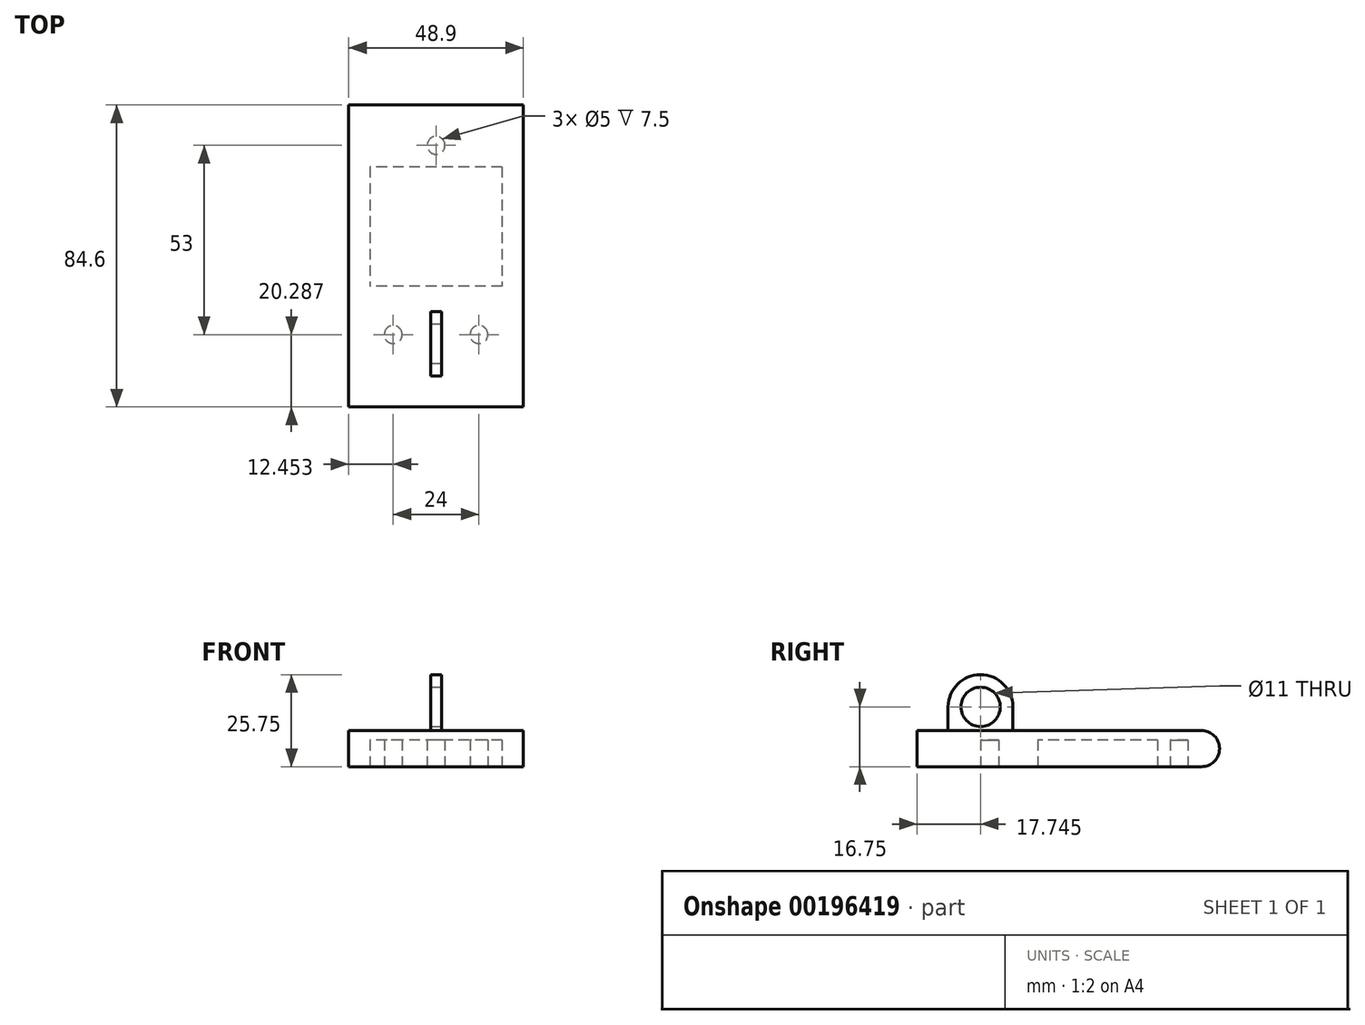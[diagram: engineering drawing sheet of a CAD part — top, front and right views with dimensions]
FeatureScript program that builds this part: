
annotation { "Feature Type Name" : "Feature", "Feature Type Description" : "" }
export const myFeature = defineFeature(function(context is Context, id is Id, definition is map)
    precondition{}
    {
        {
            var Q0;
            Q0=qCreatedBy(makeId("Top.planeOp"),FACE);
            var sketch = newSketch(context, id + "F0", { "sketchPlane" : qUnion([Q0])});
            skLineSegment(sketch, "E0.bottom", {"start": v(-0.48, 0.42) * mm, "end": v(48.42, 0.42) * mm});
            skLineSegment(sketch, "E0.top", {"start": v(-0.48, 85.02) * mm, "end": v(48.42, 85.02) * mm});
            skLineSegment(sketch, "E0.left", {"start": v(-0.48, 0.42) * mm, "end": v(-0.48, 85.02) * mm});
            skLineSegment(sketch, "E0.right", {"start": v(48.42, 0.42) * mm, "end": v(48.42, 85.02) * mm});
            skLineSegment(sketch, "E1.bottom", {"start": v(22.42, 9.07) * mm, "end": v(25.52, 9.07) * mm});
            skLineSegment(sketch, "E1.top", {"start": v(22.42, 27.17) * mm, "end": v(25.52, 27.17) * mm});
            skLineSegment(sketch, "E1.left", {"start": v(22.42, 9.07) * mm, "end": v(22.42, 27.17) * mm});
            skLineSegment(sketch, "E1.right", {"start": v(25.52, 9.07) * mm, "end": v(25.52, 27.17) * mm});
            skSolve(sketch);
        }
        {
            var Q0;
            Q0=makeQuery(id+"F0.imprint","IMPRINT",FACE,{"disambiguationData":[TD([[makeQuery(id+"F0.imprint","IMPRINT",EDGE,{"derivedFrom":sQuery(id+"F0.wireOp",EDGE,"E1.bottom")}),1.0]])]});
            extrude(context, id + "F1", {"entities" : qUnion([Q0]), "depth" : 25.75 * mm});
        }
        {
            var Q0;
            Q0=makeQuery(id+"F0.imprint","IMPRINT",FACE,{"disambiguationData":[TD([[makeQuery(id+"F0.imprint","IMPRINT",EDGE,{"derivedFrom":sQuery(id+"F0.wireOp",EDGE,"E0.bottom")}),1.0]])]});
            extrude(context, id + "F2", {"entities" : qUnion([Q0]), "operationType" : NewBodyOperationType.ADD, "depth" : 10.1 * mm});
        }
        {
            var Q0;
            Q0=makeQuery(id+"F2.opExtrude","CAP_EDGE",EDGE,{"disambiguationData":[OSD([sQuery(id+"F0.wireOp",EDGE,"E0.top")])],"isStart":false});
            var Q1;
            Q1=makeQuery(id+"F2.opExtrude","CAP_EDGE",EDGE,{"disambiguationData":[OSD([sQuery(id+"F0.wireOp",EDGE,"E0.top")])],"isStart":true});
            fillet(context, id + "F3", {"entities" : qUnion([Q0, Q1]), "radius" : 5 * mm, "tangentPropagation" : true, "allowEdgeOverflow" : false});
        }
        {
            var Q0;
            Q0=makeQuery(id+"F1.opExtrude","CAP_EDGE",EDGE,{"disambiguationData":[OSD([sQuery(id+"F0.wireOp",EDGE,"E1.bottom")])],"isStart":false});
            var Q1;
            Q1=makeQuery(id+"F1.opExtrude","CAP_EDGE",EDGE,{"disambiguationData":[OSD([sQuery(id+"F0.wireOp",EDGE,"E1.top")])],"isStart":false});
            fillet(context, id + "F4", {"entities" : qUnion([Q0, Q1]), "radius" : 9 * mm, "tangentPropagation" : true, "allowEdgeOverflow" : false});
        }
        {
            var Q0;
            Q0=makeQuery(id+"F1.opExtrude","SWEPT_FACE",FACE,{"disambiguationData":[OSD([sQuery(id+"F0.wireOp",EDGE,"E1.right")])]});
            var sketch = newSketch(context, id + "F5", { "sketchPlane" : qUnion([Q0])});
            skCircle(sketch, "E2", {"center": v(18.17, 16.75) * mm, "radius": 5.5 * mm});
            skSolve(sketch);
        }
        {
            var Q0;
            Q0=makeQuery(id+"F5.imprint","IMPRINT",FACE,{"disambiguationData":[TD([[makeQuery(id+"F5.imprint","IMPRINT",EDGE,{"derivedFrom":sQuery(id+"F5.wireOp",EDGE,"E2")}),1.0]])]});
            extrude(context, id + "F6", {"entities" : qUnion([Q0]), "operationType" : NewBodyOperationType.REMOVE, "endBound" : BoundingType.THROUGH_ALL, "oppositeDirection" : true, "depth" : 25 * mm});
        }
        {
            var Q0;
            Q0=makeQuery(id+"F0.imprint","IMPRINT",FACE,{"disambiguationData":[TD([[makeQuery(id+"F0.imprint","IMPRINT",EDGE,{"derivedFrom":sQuery(id+"F0.wireOp",EDGE,"E0.bottom")}),1.0]])]});
            var sketch = newSketch(context, id + "F7", { "sketchPlane" : qUnion([Q0])});
            skCircle(sketch, "E3", {"center": v(23.97, 73.7) * mm, "radius": 2.5 * mm});
            skCircle(sketch, "E4", {"center": v(35.97, 20.7) * mm, "radius": 2.5 * mm});
            skCircle(sketch, "E5", {"center": v(11.97, 20.7) * mm, "radius": 2.5 * mm});
            skLineSegment(sketch, "E6.bottom", {"start": v(42.47, 67.7) * mm, "end": v(5.47, 67.7) * mm});
            skLineSegment(sketch, "E6.top", {"start": v(42.47, 34.2) * mm, "end": v(5.47, 34.2) * mm});
            skLineSegment(sketch, "E6.left", {"start": v(42.47, 67.7) * mm, "end": v(42.47, 34.2) * mm});
            skLineSegment(sketch, "E6.right", {"start": v(5.47, 67.7) * mm, "end": v(5.47, 34.2) * mm});
            skSolve(sketch);
        }
        {
            var Q0;
            Q0 = qSketchRegion(id + "F7", true);
            extrude(context, id + "F8", {"entities" : qUnion([Q0]), "operationType" : NewBodyOperationType.REMOVE, "depth" : 7.5 * mm});
        }
    });
